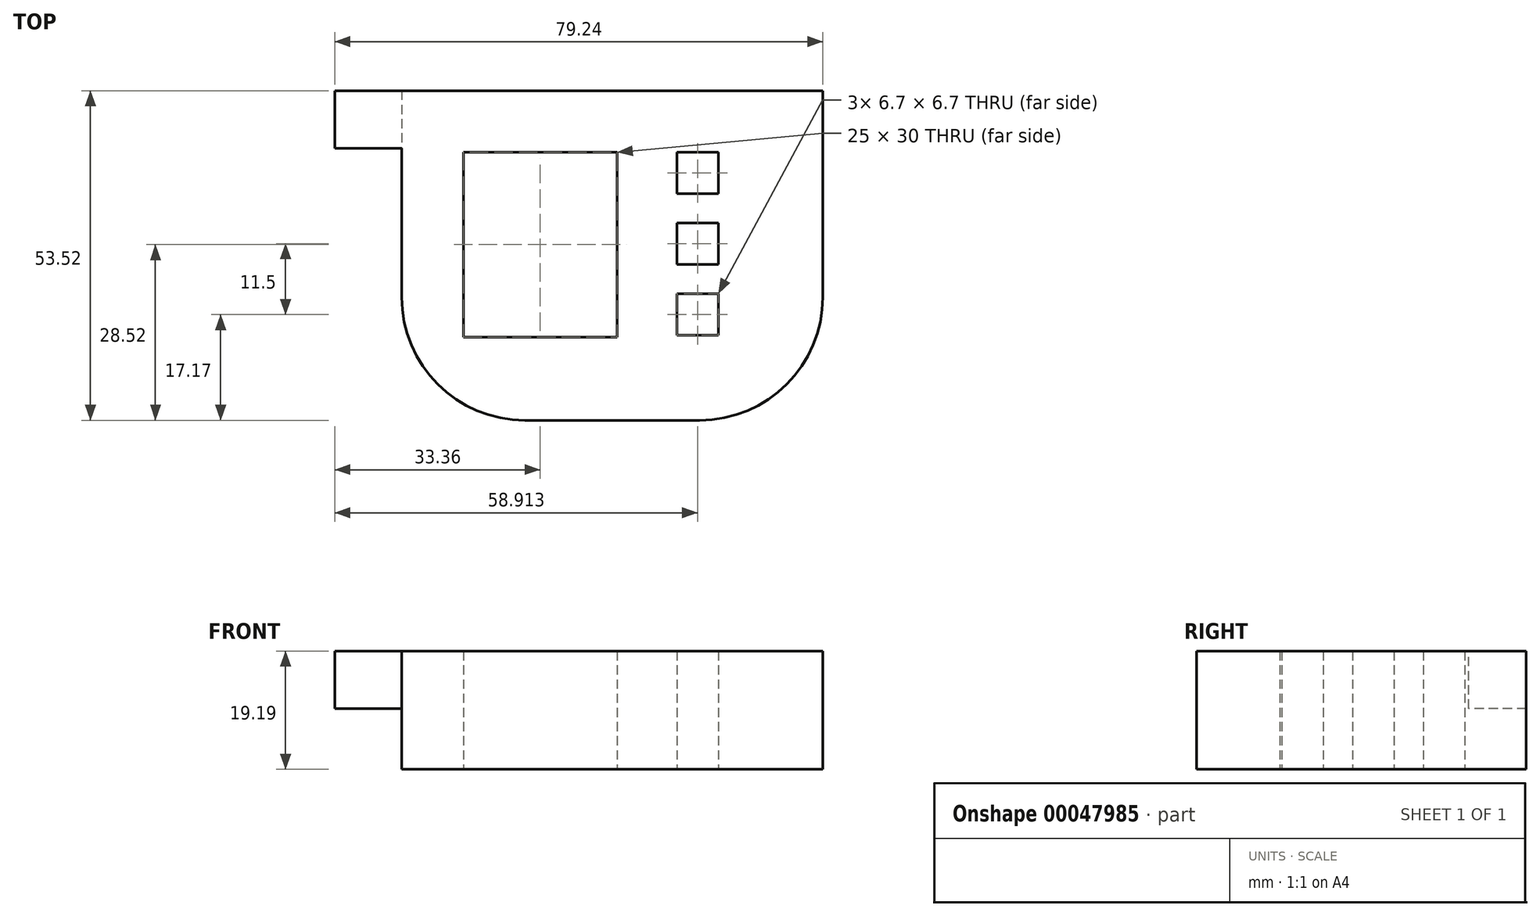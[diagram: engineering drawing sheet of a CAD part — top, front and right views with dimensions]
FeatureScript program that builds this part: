
annotation { "Feature Type Name" : "Feature", "Feature Type Description" : "" }
export const myFeature = defineFeature(function(context is Context, id is Id, definition is map)
    precondition{}
    {
        {
            var Q0;
            Q0=qCreatedBy(makeId("Top.planeOp"),FACE);
            var sketch = newSketch(context, id + "F0", { "sketchPlane" : qUnion([Q0])});
            skLineSegment(sketch, "E0.rect.bottom", {"start": v(34.19, -26.76) * mm, "end": v(-34.19, -26.76) * mm});
            skLineSegment(sketch, "E0.rect.top", {"start": v(34.19, 26.76) * mm, "end": v(-34.19, 26.76) * mm});
            skLineSegment(sketch, "E0.rect.left", {"start": v(34.19, -26.76) * mm, "end": v(34.19, 26.76) * mm});
            skLineSegment(sketch, "E0.rect.right", {"start": v(-34.19, -26.76) * mm, "end": v(-34.19, 26.76) * mm});
            skPoint(sketch, "E0.rect.middle", {"position": v(0, 0) * mm});
            skSolve(sketch);
        }
        {
            var Q0;
            Q0 = qSketchRegion(id + "F0", true);
            extrude(context, id + "F1", {"entities" : qUnion([Q0]), "depth" : 19.2 * mm});
        }
        {
            var Q0;
            Q0=makeQuery(id+"F1.opExtrude","SWEPT_FACE",FACE,{"disambiguationData":[OSD([sQuery(id+"F0.wireOp",EDGE,"E0.rect.right")])]});
            var sketch = newSketch(context, id + "F2", { "sketchPlane" : qUnion([Q0])});
            skLineSegment(sketch, "E1", {"start": v(-26.76, 19.19) * mm, "end": v(-26.76, 9.86) * mm});
            skLineSegment(sketch, "E2", {"start": v(-26.76, 9.86) * mm, "end": v(-17.43, 9.86) * mm});
            skLineSegment(sketch, "E3", {"start": v(-17.43, 9.86) * mm, "end": v(-17.43, 19.19) * mm});
            skSolve(sketch);
        }
        {
            var Q0;
            {var subQ0=sQuery(id+"F2.wireOp",EDGE,"E1");Q0=makeQuery(id+"F2.imprint","IMPRINT",FACE,{"disambiguationData":[TD([[makeQuery(id+"F2.imprint","IMPRINT",EDGE,{"derivedFrom":subQ0}),1.0]])]});}
            extrude(context, id + "F3", {"entities" : qUnion([Q0]), "operationType" : NewBodyOperationType.ADD, "depth" : 10.86 * mm});
        }
        {
            var Q0;
            Q0=makeQuery(id+"F1.opExtrude","SWEPT_EDGE",EDGE,{"disambiguationData":[OSD([sQuery(id+"F0.wireOp",EDGE,"E0.rect.bottom"),sQuery(id+"F0.wireOp",EDGE,"E0.rect.left")])]});
            fillet(context, id + "F4", {"entities" : qUnion([Q0]), "radius" : 20 * mm, "tangentPropagation" : true, "allowEdgeOverflow" : false});
        }
        {
            var Q0;
            Q0=makeQuery(id+"F1.opExtrude","SWEPT_EDGE",EDGE,{"disambiguationData":[OSD([sQuery(id+"F0.wireOp",EDGE,"E0.rect.bottom"),sQuery(id+"F0.wireOp",EDGE,"E0.rect.right")])]});
            fillet(context, id + "F5", {"entities" : qUnion([Q0]), "radius" : 20 * mm, "tangentPropagation" : true, "allowEdgeOverflow" : false});
        }
        {
            var Q0;
            Q0=makeQuery(id+"F3.boolean.opBoolean","MERGE",FACE,{"derivedFrom":[makeQuery(id+"F1.opExtrude","SWEPT_FACE",FACE,{"disambiguationData":[OSD([sQuery(id+"F0.wireOp",EDGE,"E0.rect.top")])]}),makeQuery(id+"F3.opExtrude","SWEPT_FACE",FACE,{"disambiguationData":[OSD([sQuery(id+"F2.wireOp",EDGE,"E1")])]})]});
            var sketch = newSketch(context, id + "F6", { "sketchPlane" : qUnion([Q0])});
            skLineSegment(sketch, "E4.bottom", {"start": v(0, 1.09) * mm, "end": v(-33.14, 1.09) * mm});
            skLineSegment(sketch, "E4.top", {"start": v(0, 17.61) * mm, "end": v(-33.14, 17.61) * mm});
            skLineSegment(sketch, "E4.left", {"start": v(0, 1.09) * mm, "end": v(0, 17.61) * mm});
            skLineSegment(sketch, "E4.right", {"start": v(-33.14, 1.09) * mm, "end": v(-33.14, 17.61) * mm});
            skSolve(sketch);
        }
        {
            var Q0;
            Q0=makeQuery(id+"F0.imprint","IMPRINT",FACE,{"disambiguationData":[TD([[makeQuery(id+"F0.imprint","IMPRINT",EDGE,{"derivedFrom":sQuery(id+"F0.wireOp",EDGE,"E0.rect.bottom")}),-1.0]])]});
            var sketch = newSketch(context, id + "F7", { "sketchPlane" : qUnion([Q0])});
            skLineSegment(sketch, "E5.bottom", {"start": v(-24.19, -13.24) * mm, "end": v(0.81, -13.24) * mm});
            skLineSegment(sketch, "E5.top", {"start": v(-24.19, 16.76) * mm, "end": v(0.81, 16.76) * mm});
            skLineSegment(sketch, "E5.left", {"start": v(-24.19, -13.24) * mm, "end": v(-24.19, 16.76) * mm});
            skLineSegment(sketch, "E5.right", {"start": v(0.81, -13.24) * mm, "end": v(0.81, 16.76) * mm});
            skLineSegment(sketch, "E6.bottom", {"start": v(10.51, 10.06) * mm, "end": v(17.21, 10.06) * mm});
            skLineSegment(sketch, "E6.top", {"start": v(10.51, 16.76) * mm, "end": v(17.21, 16.76) * mm});
            skLineSegment(sketch, "E6.left", {"start": v(10.51, 10.06) * mm, "end": v(10.51, 16.76) * mm});
            skLineSegment(sketch, "E6.right", {"start": v(17.21, 10.06) * mm, "end": v(17.21, 16.76) * mm});
            skLineSegment(sketch, "E7.0.1.0", {"start": v(10.51, -1.44) * mm, "end": v(10.51, 5.26) * mm});
            skLineSegment(sketch, "E7.0.1.1", {"start": v(10.51, -1.44) * mm, "end": v(17.21, -1.44) * mm});
            skLineSegment(sketch, "E7.0.1.2", {"start": v(17.21, -1.44) * mm, "end": v(17.21, 5.26) * mm});
            skLineSegment(sketch, "E7.0.1.3", {"start": v(10.51, 5.26) * mm, "end": v(17.21, 5.26) * mm});
            skLineSegment(sketch, "E7.0.2.0", {"start": v(10.51, -12.94) * mm, "end": v(10.51, -6.24) * mm});
            skLineSegment(sketch, "E7.0.2.1", {"start": v(10.51, -12.94) * mm, "end": v(17.21, -12.94) * mm});
            skLineSegment(sketch, "E7.0.2.2", {"start": v(17.21, -12.94) * mm, "end": v(17.21, -6.24) * mm});
            skLineSegment(sketch, "E7.0.2.3", {"start": v(10.51, -6.24) * mm, "end": v(17.21, -6.24) * mm});
            skLineSegment(sketch, "E7.direction1", {"start": v(10.51, 10.06) * mm, "end": v(35.51, 10.06) * mm, "construction": true});
            skLineSegment(sketch, "E7.direction2", {"start": v(10.51, 10.06) * mm, "end": v(10.51, -1.44) * mm, "construction": true});
            skSolve(sketch);
        }
        {
            var Q0;
            Q0 = qSketchRegion(id + "F7", true);
            extrude(context, id + "F8", {"entities" : qUnion([Q0]), "operationType" : NewBodyOperationType.REMOVE, "depth" : 29.55 * mm});
        }
    });
